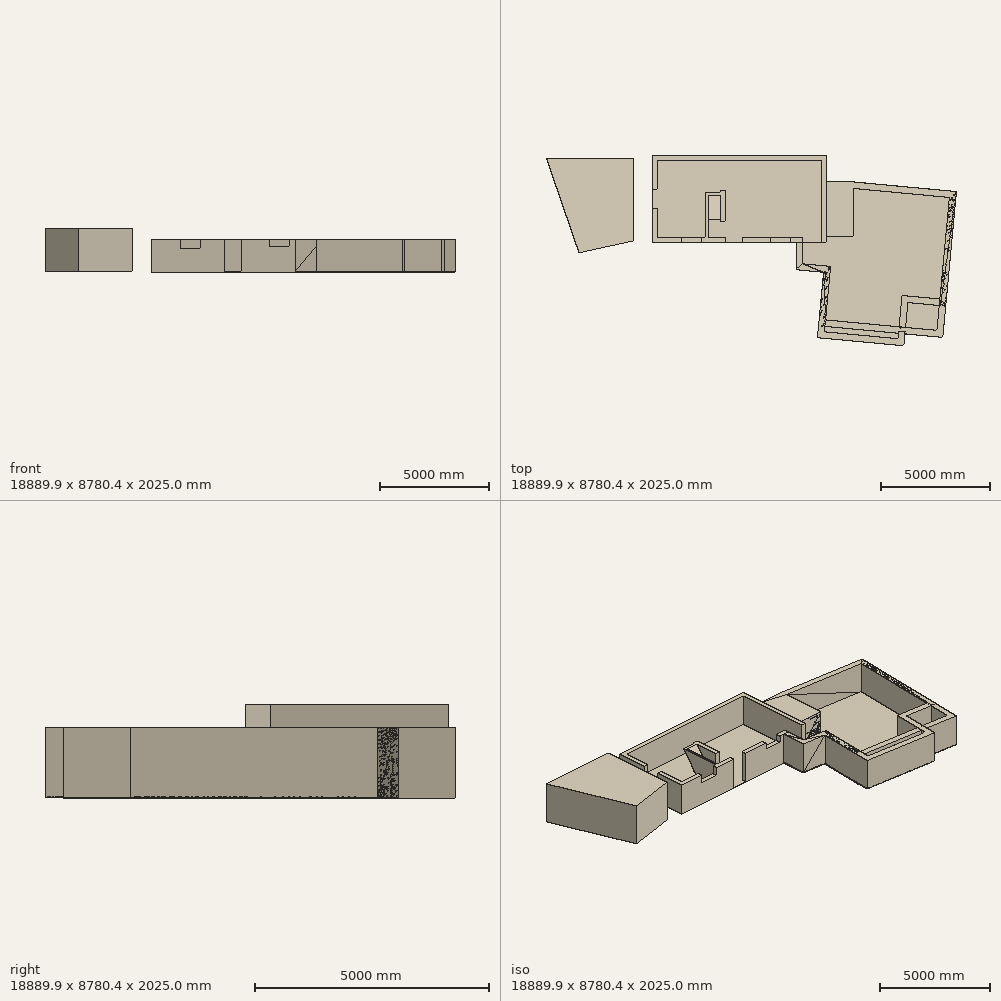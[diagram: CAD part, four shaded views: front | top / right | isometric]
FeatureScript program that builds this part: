
annotation { "Feature Type Name" : "Feature", "Feature Type Description" : "" }
export const myFeature = defineFeature(function(context is Context, id is Id, definition is map)
    precondition{}
    {
        {
            var Q0;
            Q0=qCreatedBy(makeId("Top.planeOp"),FACE);
            var sketch = newSketch(context, id + "F0", { "sketchPlane" : qUnion([Q0])});
            skLineSegment(sketch, "E0.bottom", {"start": v(0, 0) * mm, "end": v(8000, 0) * mm});
            skLineSegment(sketch, "E0.top", {"start": v(0, 4000) * mm, "end": v(8000, 4000) * mm});
            skLineSegment(sketch, "E0.left", {"start": v(0, 0) * mm, "end": v(0, 4000) * mm});
            skLineSegment(sketch, "E0.right", {"start": v(8000, 0) * mm, "end": v(8000, 4000) * mm});
            skPoint(sketch, "E1", {"position": v(8000, 3790) * mm});
            skPoint(sketch, "E2", {"position": v(8781.4, 3726.12) * mm});
            skLineSegment(sketch, "E3", {"start": v(8000, 3790) * mm, "end": v(8781.4, 3726.12) * mm});
            skPoint(sketch, "E4", {"position": v(8821.2, 4094.98) * mm});
            skLineSegment(sketch, "E5", {"start": v(8781.4, 3726.12) * mm, "end": v(8821.2, 4094.98) * mm});
            skPoint(sketch, "E6", {"position": v(11874.29, 3808.86) * mm});
            skPoint(sketch, "E7", {"position": v(11736, -546) * mm});
            skPoint(sketch, "E8", {"position": v(8636, -546) * mm});
            skPoint(sketch, "E9", {"position": v(8636, 269) * mm});
            skPoint(sketch, "E10", {"position": v(8000, 269) * mm});
            skLineSegment(sketch, "E11", {"start": v(8821.2, 4094.98) * mm, "end": v(11874.29, 3808.86) * mm});
            skLineSegment(sketch, "E12", {"start": v(11874.29, 3808.86) * mm, "end": v(11736, -546) * mm});
            skLineSegment(sketch, "E13", {"start": v(11736, -546) * mm, "end": v(8636, -546) * mm});
            skLineSegment(sketch, "E14", {"start": v(8636, -546) * mm, "end": v(8636, 269) * mm});
            skLineSegment(sketch, "E15", {"start": v(8636, 269) * mm, "end": v(8000, 269) * mm});
            skLineSegment(sketch, "E16", {"start": v(8636, 269) * mm, "end": v(9250, 269) * mm});
            skLineSegment(sketch, "E17", {"start": v(9250, 269) * mm, "end": v(9250, 990) * mm});
            skLineSegment(sketch, "E18", {"start": v(9250, 990) * mm, "end": v(9763, 990) * mm});
            skLineSegment(sketch, "E19", {"start": v(9763, 990) * mm, "end": v(9763, 1490) * mm});
            skLineSegment(sketch, "E20", {"start": v(9763, 1490) * mm, "end": v(9250, 1490) * mm});
            skLineSegment(sketch, "E21", {"start": v(9250, 1490) * mm, "end": v(9250, 2769) * mm});
            skLineSegment(sketch, "E22", {"start": v(9250, 2769) * mm, "end": v(8000, 2769) * mm});
            skLineSegment(sketch, "E23", {"start": v(11874.29, 3808.86) * mm, "end": v(14303.17, 3581.23) * mm});
            skLineSegment(sketch, "E24", {"start": v(14303.17, 3581.23) * mm, "end": v(14605.98, 6812.25) * mm});
            skLineSegment(sketch, "E25", {"start": v(8821.2, 4094.98) * mm, "end": v(9124, 7326) * mm});
            skPoint(sketch, "E26", {"position": v(6355, 0) * mm});
            skPoint(sketch, "E27", {"position": v(5445, 0) * mm});
            skPoint(sketch, "E28", {"position": v(4130, 0) * mm});
            skPoint(sketch, "E29", {"position": v(3370, 0) * mm});
            skPoint(sketch, "E30", {"position": v(2265, 0) * mm});
            skPoint(sketch, "E31", {"position": v(1305, 0) * mm});
            skLineSegment(sketch, "E32", {"start": v(9124, 7326) * mm, "end": v(14605.98, 6812.25) * mm});
            skPoint(sketch, "E33", {"position": v(0, 2435) * mm});
            skPoint(sketch, "E34", {"position": v(0, 1565) * mm});
            skSolve(sketch);
        }
        {
            var Q0;
            Q0=qCreatedBy(makeId("Top.planeOp"),FACE);
            var sketch = newSketch(context, id + "F1", { "sketchPlane" : qUnion([Q0])});
            skLineSegment(sketch, "E35", {"start": v(9250, 2769) * mm, "end": v(13993.04, 2324.5) * mm});
            skLineSegment(sketch, "E36", {"start": v(13993.04, 2324.5) * mm, "end": v(13363.21, -4396.06) * mm});
            skLineSegment(sketch, "E37", {"start": v(13363.21, -4396.06) * mm, "end": v(7638.3, -3859.53) * mm});
            skLineSegment(sketch, "E38", {"start": v(7638.3, -3859.53) * mm, "end": v(7869.37, -1393.9) * mm});
            skLineSegment(sketch, "E39", {"start": v(9250, 2769) * mm, "end": v(8000, 2769) * mm});
            skLineSegment(sketch, "E40", {"start": v(8000, 2769) * mm, "end": v(8000, 0) * mm});
            skLineSegment(sketch, "E41", {"start": v(6600, 0) * mm, "end": v(8000, 0) * mm});
            skLineSegment(sketch, "E42", {"start": v(6600, 0) * mm, "end": v(6600, -1274.93) * mm});
            skLineSegment(sketch, "E43", {"start": v(6600, -1274.93) * mm, "end": v(7869.37, -1393.9) * mm});
            skSolve(sketch);
        }
        {
            var Q0;
            Q0=qCreatedBy(makeId("Top.planeOp"),FACE);
            var sketch = newSketch(context, id + "F2", { "sketchPlane" : qUnion([Q0])});
            skLineSegment(sketch, "E44.0", {"start": v(9250, 2467.69) * mm, "end": v(13666.36, 2053.8) * mm});
            skLineSegment(sketch, "E44.1", {"start": v(13666.36, 2053.8) * mm, "end": v(13092.51, -4069.37) * mm});
            skLineSegment(sketch, "E44.2", {"start": v(6900, 0) * mm, "end": v(6900, -1001.73) * mm});
            skLineSegment(sketch, "E44.3", {"start": v(6900, -1001.73) * mm, "end": v(8196.05, -1123.2) * mm});
            skLineSegment(sketch, "E44.4", {"start": v(7964.98, -3588.83) * mm, "end": v(8196.05, -1123.2) * mm});
            skLineSegment(sketch, "E44.5", {"start": v(13092.51, -4069.37) * mm, "end": v(7964.98, -3588.83) * mm});
            skLineSegment(sketch, "E45.0", {"start": v(9250, 2769) * mm, "end": v(13993.04, 2324.5) * mm});
            skLineSegment(sketch, "E46.0", {"start": v(13993.04, 2324.5) * mm, "end": v(13363.21, -4396.06) * mm});
            skLineSegment(sketch, "E47.0", {"start": v(13363.21, -4396.06) * mm, "end": v(7638.3, -3859.53) * mm});
            skLineSegment(sketch, "E48.0", {"start": v(7638.3, -3859.53) * mm, "end": v(7869.37, -1393.9) * mm});
            skLineSegment(sketch, "E49.0", {"start": v(6600, -1274.93) * mm, "end": v(7869.37, -1393.9) * mm});
            skLineSegment(sketch, "E50.0", {"start": v(6600, 0) * mm, "end": v(6600, -1274.93) * mm});
            skLineSegment(sketch, "E51", {"start": v(6600, 0) * mm, "end": v(6900, 0) * mm});
            skLineSegment(sketch, "E52", {"start": v(9250, 2467.69) * mm, "end": v(9250, 269) * mm});
            skLineSegment(sketch, "E53", {"start": v(9250, 269) * mm, "end": v(8000, 269) * mm});
            skLineSegment(sketch, "E54", {"start": v(8000, 269) * mm, "end": v(8000, 2769) * mm});
            skLineSegment(sketch, "E55", {"start": v(8000, 2769) * mm, "end": v(9250, 2769) * mm});
            skSolve(sketch);
        }
        {
            var Q0;
            Q0=qCreatedBy(makeId("Top.planeOp"),FACE);
            var sketch = newSketch(context, id + "F3", { "sketchPlane" : qUnion([Q0])});
            skLineSegment(sketch, "E56.0", {"start": v(0, 4000) * mm, "end": v(8000, 4000) * mm});
            skLineSegment(sketch, "E57.0", {"start": v(0, 0) * mm, "end": v(0, 4000) * mm});
            skLineSegment(sketch, "E58.0", {"start": v(0, 0) * mm, "end": v(6900, 0) * mm});
            skLineSegment(sketch, "E59.0", {"start": v(8000, 0) * mm, "end": v(8000, 4000) * mm});
            skLineSegment(sketch, "E60.0", {"start": v(230, 3770) * mm, "end": v(7770, 3770) * mm});
            skLineSegment(sketch, "E60.1", {"start": v(230, 230) * mm, "end": v(230, 3770) * mm});
            skLineSegment(sketch, "E60.2", {"start": v(230, 230) * mm, "end": v(2430, 230) * mm});
            skLineSegment(sketch, "E60.3", {"start": v(7770, 0) * mm, "end": v(7770, 3770) * mm});
            skLineSegment(sketch, "E61.1", {"start": v(0, 4000) * mm, "end": v(0, 0) * mm});
            skLineSegment(sketch, "E61.2", {"start": v(8000, 269) * mm, "end": v(8000, 2769) * mm});
            skLineSegment(sketch, "E61.3", {"start": v(8000, 2769) * mm, "end": v(8000, 3790) * mm});
            skLineSegment(sketch, "E61.4", {"start": v(8000, 3790) * mm, "end": v(8000, 4000) * mm});
            skLineSegment(sketch, "E61.5", {"start": v(8000, 0) * mm, "end": v(8000, 269) * mm});
            skLineSegment(sketch, "E61.6", {"start": v(8000, 4000) * mm, "end": v(0, 4000) * mm});
            skLineSegment(sketch, "E62", {"start": v(6900, 0) * mm, "end": v(6900, 230) * mm});
            skLineSegment(sketch, "E63.trimOffspring", {"start": v(8000, 0) * mm, "end": v(8000, 0) * mm});
            skLineSegment(sketch, "E64.trimOffspring", {"start": v(7770, 0) * mm, "end": v(8000, 0) * mm});
            skLineSegment(sketch, "E65", {"start": v(3370, 2370) * mm, "end": v(3370, 940) * mm});
            skLineSegment(sketch, "E66", {"start": v(3140, 2370) * mm, "end": v(3370, 2370) * mm});
            skLineSegment(sketch, "E67", {"start": v(2430, 230) * mm, "end": v(2430, 1170) * mm});
            skLineSegment(sketch, "E68", {"start": v(2545, 1170) * mm, "end": v(2545, 230) * mm});
            skLineSegment(sketch, "E69.trimOffspring", {"start": v(3140, 940) * mm, "end": v(3140, 2370) * mm});
            skLineSegment(sketch, "E70.trimOffspring", {"start": v(2545, 230) * mm, "end": v(6900, 230) * mm});
            skPoint(sketch, "E71.start.orphan", {"position": v(2545, 230) * mm});
            skLineSegment(sketch, "E72", {"start": v(2430, 1170) * mm, "end": v(2545, 1170) * mm});
            skLineSegment(sketch, "E73", {"start": v(3140, 940) * mm, "end": v(3370, 940) * mm});
            skSolve(sketch);
        }
        {
            var Q0;
            Q0 = qSketchRegion(id + "F2", true);
            extrude(context, id + "F4", {"entities" : qUnion([Q0]), "depth" : 1500 * mm});
        }
        {
            var Q0;
            Q0 = qSketchRegion(id + "F3", true);
            extrude(context, id + "F5", {"entities" : qUnion([Q0]), "depth" : 1500 * mm});
        }
        {
            var Q0;
            Q0=makeQuery(id+"F5.opExtrude","SWEPT_FACE",FACE,{"disambiguationData":[OSD([sQuery(id+"F3.wireOp",EDGE,"E58.0")])]});
            var sketch = newSketch(context, id + "F6", { "sketchPlane" : qUnion([Q0])});
            skLineSegment(sketch, "E74.bottom", {"start": v(3370, 0) * mm, "end": v(4130, 0) * mm});
            skLineSegment(sketch, "E74.top", {"start": v(3370, 1500) * mm, "end": v(4130, 1500) * mm});
            skLineSegment(sketch, "E74.left", {"start": v(3370, 0) * mm, "end": v(3370, 1500) * mm});
            skLineSegment(sketch, "E74.right", {"start": v(4130, 0) * mm, "end": v(4130, 1500) * mm});
            skLineSegment(sketch, "E75.bottom", {"start": v(5445, 1500) * mm, "end": v(6355, 1500) * mm});
            skLineSegment(sketch, "E75.top", {"start": v(5445, 1175) * mm, "end": v(6355, 1175) * mm});
            skLineSegment(sketch, "E75.left", {"start": v(5445, 1500) * mm, "end": v(5445, 1175) * mm});
            skLineSegment(sketch, "E75.right", {"start": v(6355, 1500) * mm, "end": v(6355, 1175) * mm});
            skLineSegment(sketch, "E76.bottom", {"start": v(1305, 1500) * mm, "end": v(2265, 1500) * mm});
            skLineSegment(sketch, "E76.top", {"start": v(1305, 1098) * mm, "end": v(2265, 1098) * mm});
            skLineSegment(sketch, "E76.left", {"start": v(1305, 1500) * mm, "end": v(1305, 1098) * mm});
            skLineSegment(sketch, "E76.right", {"start": v(2265, 1500) * mm, "end": v(2265, 1098) * mm});
            skSolve(sketch);
        }
        {
            var Q0;
            Q0 = qSketchRegion(id + "F6", true);
            extrude(context, id + "F7", {"entities" : qUnion([Q0]), "operationType" : NewBodyOperationType.REMOVE, "endBound" : BoundingType.UP_TO_NEXT, "oppositeDirection" : true, "depth" : 25 * mm});
        }
        {
            var Q0;
            {var subQ1=sQuery(id+"F0.wireOp",EDGE,"E0.bottom");Q0=makeQuery(id+"F0.imprint","IMPRINT",FACE,{"disambiguationData":[TD([[makeQuery(id+"F0.imprint","IMPRINT",EDGE,{"derivedFrom":subQ1}),1.0]])]});}
            extrude(context, id + "F8", {"entities" : qUnion([Q0]), "oppositeDirection" : true, "depth" : 25 * mm});
        }
        {
            var Q0;
            Q0=makeQuery(id+"F8.opExtrude","SWEPT_BODY",BODY,{"disambiguationData":[OSD([sQuery(id+"F0.wireOp",EDGE,"E0.bottom"),sQuery(id+"F0.wireOp",EDGE,"E0.top"),sQuery(id+"F0.wireOp",EDGE,"E0.left"),sQuery(id+"F0.wireOp",EDGE,"E0.right")])]});
            var Q1;
            Q1=makeQuery(id+"F7.boolean.opBoolean","SPLIT",BODY,{"disambiguationData":[OD(1.0)],"derivedFrom":makeQuery(id+"F5.opExtrude","SWEPT_BODY",BODY,{"disambiguationData":[OSD([sQuery(id+"F3.wireOp",EDGE,"E60.0"),sQuery(id+"F3.wireOp",EDGE,"E60.1"),sQuery(id+"F3.wireOp",EDGE,"E60.2"),sQuery(id+"F3.wireOp",EDGE,"E60.3"),sQuery(id+"F3.wireOp",EDGE,"E58.0"),sQuery(id+"F3.wireOp",EDGE,"E61.1"),sQuery(id+"F3.wireOp",EDGE,"E61.2"),sQuery(id+"F3.wireOp",EDGE,"E61.3"),sQuery(id+"F3.wireOp",EDGE,"E61.4"),sQuery(id+"F3.wireOp",EDGE,"E61.5"),sQuery(id+"F3.wireOp",EDGE,"E61.6"),sQuery(id+"F3.wireOp",EDGE,"E62"),sQuery(id+"F3.wireOp",EDGE,"E64.trimOffspring")])]})});
            var Q2;
            Q2=makeQuery(id+"F7.boolean.opBoolean","SPLIT",BODY,{"disambiguationData":[OD(0.0)],"derivedFrom":makeQuery(id+"F5.opExtrude","SWEPT_BODY",BODY,{"disambiguationData":[OSD([sQuery(id+"F3.wireOp",EDGE,"E60.0"),sQuery(id+"F3.wireOp",EDGE,"E60.1"),sQuery(id+"F3.wireOp",EDGE,"E60.2"),sQuery(id+"F3.wireOp",EDGE,"E60.3"),sQuery(id+"F3.wireOp",EDGE,"E58.0"),sQuery(id+"F3.wireOp",EDGE,"E61.1"),sQuery(id+"F3.wireOp",EDGE,"E61.2"),sQuery(id+"F3.wireOp",EDGE,"E61.3"),sQuery(id+"F3.wireOp",EDGE,"E61.4"),sQuery(id+"F3.wireOp",EDGE,"E61.5"),sQuery(id+"F3.wireOp",EDGE,"E61.6"),sQuery(id+"F3.wireOp",EDGE,"E62"),sQuery(id+"F3.wireOp",EDGE,"E64.trimOffspring")])]})});
            booleanBodies(context, id + "F9", {"operationType" : BooleanOperationType.UNION, "tools" : qUnion([Q0, Q1, Q2])});
        }
        {
            var Q0;
            Q0=makeQuery(id+"F1.imprint","IMPRINT",FACE,{"disambiguationData":[TD([[makeQuery(id+"F1.imprint","IMPRINT",EDGE,{"derivedFrom":sQuery(id+"F1.wireOp",EDGE,"E35")}),-1.0]])]});
            extrude(context, id + "F10", {"entities" : qUnion([Q0]), "oppositeDirection" : true, "depth" : 25 * mm});
        }
        {
            var Q0;
            Q0=makeQuery(id+"F5.opExtrude","SWEPT_FACE",FACE,{"disambiguationData":[OSD([sQuery(id+"F3.wireOp",EDGE,"E67")])]});
            var sketch = newSketch(context, id + "F11", { "sketchPlane" : qUnion([Q0])});
            skLineSegment(sketch, "E77", {"start": v(-1170, 0) * mm, "end": v(-1170, 1500) * mm});
            skLineSegment(sketch, "E78", {"start": v(-1170, 1500) * mm, "end": v(-2295, 1500) * mm});
            skLineSegment(sketch, "E79", {"start": v(-2295, 1500) * mm, "end": v(-1170, 0) * mm});
            skPoint(sketch, "E80", {"position": v(-2370, 1600) * mm});
            skSolve(sketch);
        }
        {
            var Q0;
            Q0 = qSketchRegion(id + "F11", true);
            var Q1;
            Q1=makeQuery(id+"F5.opExtrude","SWEPT_FACE",FACE,{"disambiguationData":[OSD([sQuery(id+"F3.wireOp",EDGE,"E68")])]});
            extrude(context, id + "F12", {"entities" : qUnion([Q0]), "operationType" : NewBodyOperationType.ADD, "endBound" : BoundingType.UP_TO_SURFACE, "oppositeDirection" : true, "endBoundEntityFace" : qUnion([Q1]), "depth" : 25 * mm});
        }
        {
            var Q0;
            {var subQ0=sQuery(id+"F3.wireOp",EDGE,"E68");Q0=makeQuery(id+"F12.boolean.opBoolean","MERGE",FACE,{"derivedFrom":[makeQuery(id+"F5.opExtrude","SWEPT_FACE",FACE,{"disambiguationData":[OSD([subQ0])]}),makeQuery(id+"F12.opExtrude","CAP_FACE",FACE,{"disambiguationData":[OSD([subQ0])],"isStart":false})]});}
            var sketch = newSketch(context, id + "F13", { "sketchPlane" : qUnion([Q0])});
            skLineSegment(sketch, "E81", {"start": v(2295, 1500) * mm, "end": v(2151.25, 1500) * mm});
            skLineSegment(sketch, "E82", {"start": v(2151.25, 1500) * mm, "end": v(1026.25, 0) * mm});
            skLineSegment(sketch, "E83", {"start": v(1026.25, 0) * mm, "end": v(1170, 0) * mm});
            skLineSegment(sketch, "E84", {"start": v(1170, 0) * mm, "end": v(2295, 1500) * mm});
            skSolve(sketch);
        }
        {
            var Q0;
            Q0 = qSketchRegion(id + "F13", true);
            extrude(context, id + "F14", {"entities" : qUnion([Q0]), "operationType" : NewBodyOperationType.ADD, "endBound" : BoundingType.UP_TO_NEXT, "depth" : 25 * mm});
        }
        {
            var Q0;
            Q0=makeQuery(id+"F9.opBoolean","MERGE",FACE,{"derivedFrom":[makeQuery(id+"F5.opExtrude","SWEPT_FACE",FACE,{"disambiguationData":[OSD([sQuery(id+"F3.wireOp",EDGE,"E61.1")])]}),makeQuery(id+"F8.opExtrude","SWEPT_FACE",FACE,{"disambiguationData":[OSD([sQuery(id+"F0.wireOp",EDGE,"E0.left")])]})]});
            var sketch = newSketch(context, id + "F15", { "sketchPlane" : qUnion([Q0])});
            skLineSegment(sketch, "E85.bottom", {"start": v(-1565, 0) * mm, "end": v(-2435, 0) * mm});
            skLineSegment(sketch, "E85.top", {"start": v(-1565, 1500) * mm, "end": v(-2435, 1500) * mm});
            skLineSegment(sketch, "E85.left", {"start": v(-1565, 0) * mm, "end": v(-1565, 1500) * mm});
            skLineSegment(sketch, "E85.right", {"start": v(-2435, 0) * mm, "end": v(-2435, 1500) * mm});
            skSolve(sketch);
        }
        {
            var Q0;
            Q0=makeQuery(id+"F15.imprint","IMPRINT",FACE,{"disambiguationData":[TD([[makeQuery(id+"F15.imprint","IMPRINT",EDGE,{"derivedFrom":sQuery(id+"F15.wireOp",EDGE,"E85.bottom")}),-1.0]])]});
            extrude(context, id + "F16", {"entities" : qUnion([Q0]), "operationType" : NewBodyOperationType.REMOVE, "oppositeDirection" : true, "depth" : 230 * mm});
        }
        {
            var Q0;
            Q0=qCreatedBy(makeId("Top.planeOp"),FACE);
            var sketch = newSketch(context, id + "F17", { "sketchPlane" : qUnion([Q0])});
            skLineSegment(sketch, "E86", {"start": v(9250, 2769) * mm, "end": v(13993.04, 2324.5) * mm});
            skLineSegment(sketch, "E87", {"start": v(13993.04, 2324.5) * mm, "end": v(13498.5, -2952.38) * mm});
            skLineSegment(sketch, "E88", {"start": v(13498.5, -2952.38) * mm, "end": v(11756.14, -2789.1) * mm});
            skLineSegment(sketch, "E89", {"start": v(11756.14, -2789.1) * mm, "end": v(11569.53, -4780.37) * mm});
            skLineSegment(sketch, "E90", {"start": v(11569.53, -4780.37) * mm, "end": v(7586.98, -4407.13) * mm});
            skLineSegment(sketch, "E91", {"start": v(7586.98, -4407.13) * mm, "end": v(7869.37, -1393.9) * mm});
            skLineSegment(sketch, "E92", {"start": v(7869.37, -1393.9) * mm, "end": v(6600, -1274.93) * mm});
            skLineSegment(sketch, "E93", {"start": v(6600, -1274.93) * mm, "end": v(6600, 0) * mm});
            skLineSegment(sketch, "E94", {"start": v(6600, 0) * mm, "end": v(8000, 0) * mm});
            skLineSegment(sketch, "E95", {"start": v(8000, 0) * mm, "end": v(8000, 269) * mm});
            skLineSegment(sketch, "E96", {"start": v(8000, 269) * mm, "end": v(8000, 2769) * mm});
            skLineSegment(sketch, "E97", {"start": v(8000, 2769) * mm, "end": v(9250, 2769) * mm});
            skSolve(sketch);
        }
        {
            var Q0;
            Q0 = qSketchRegion(id + "F17", true);
            extrude(context, id + "F18", {"entities" : qUnion([Q0]), "depth" : 25 * mm, "offsetDistance" : 25 * mm});
        }
        {
            var Q0;
            Q0=qCreatedBy(makeId("Top.planeOp"),FACE);
            var sketch = newSketch(context, id + "F19", { "sketchPlane" : qUnion([Q0])});
            skLineSegment(sketch, "E98.0", {"start": v(6900, 0) * mm, "end": v(6900, -1001.73) * mm});
            skLineSegment(sketch, "E98.1", {"start": v(6900, -1001.73) * mm, "end": v(8196.05, -1123.2) * mm});
            skLineSegment(sketch, "E98.2", {"start": v(9250, 2467.69) * mm, "end": v(13666.36, 2053.8) * mm});
            skLineSegment(sketch, "E99", {"start": v(8000, 269) * mm, "end": v(9250, 269) * mm});
            skLineSegment(sketch, "E100", {"start": v(9250, 269) * mm, "end": v(9250, 2467.69) * mm});
            skLineSegment(sketch, "E101.0", {"start": v(9250, 2769) * mm, "end": v(8000, 2769) * mm});
            skLineSegment(sketch, "E102.0", {"start": v(9250, 2769) * mm, "end": v(13993.04, 2324.5) * mm});
            skLineSegment(sketch, "E103.0", {"start": v(6600, -1274.93) * mm, "end": v(7869.37, -1393.9) * mm});
            skLineSegment(sketch, "E104.0", {"start": v(6600, 0) * mm, "end": v(6600, -1274.93) * mm});
            skLineSegment(sketch, "E105", {"start": v(6600, 0) * mm, "end": v(6900, 0) * mm});
            skLineSegment(sketch, "E106", {"start": v(8000, 269) * mm, "end": v(8000, 2769) * mm});
            skLineSegment(sketch, "E107.0", {"start": v(13993.04, 2324.5) * mm, "end": v(13498.5, -2952.38) * mm});
            skLineSegment(sketch, "E108.0", {"start": v(13498.5, -2952.38) * mm, "end": v(11756.14, -2789.1) * mm});
            skLineSegment(sketch, "E109.0", {"start": v(11756.14, -2789.1) * mm, "end": v(11569.53, -4780.37) * mm});
            skLineSegment(sketch, "E110.0", {"start": v(11569.53, -4780.37) * mm, "end": v(7586.98, -4407.13) * mm});
            skLineSegment(sketch, "E111.0", {"start": v(7586.98, -4407.13) * mm, "end": v(7869.37, -1393.9) * mm});
            skLineSegment(sketch, "E112.0", {"start": v(7913.66, -4136.44) * mm, "end": v(8196.05, -1123.2) * mm});
            skLineSegment(sketch, "E112.1", {"start": v(13666.36, 2053.8) * mm, "end": v(13227.8, -2625.7) * mm});
            skLineSegment(sketch, "E112.2", {"start": v(13227.8, -2625.7) * mm, "end": v(11485.44, -2462.4) * mm});
            skLineSegment(sketch, "E112.3", {"start": v(11485.44, -2462.4) * mm, "end": v(11298.83, -4453.68) * mm});
            skLineSegment(sketch, "E112.4", {"start": v(11298.83, -4453.68) * mm, "end": v(7913.66, -4136.44) * mm});
            skSolve(sketch);
        }
        {
            var Q0;
            Q0 = qSketchRegion(id + "F19", true);
            extrude(context, id + "F20", {"entities" : qUnion([Q0]), "depth" : 1500 * mm, "offsetDistance" : 25 * mm});
        }
        {
            var Q0;
            Q0=qCreatedBy(makeId("Top.planeOp"),FACE);
            var sketch = newSketch(context, id + "F21", { "sketchPlane" : qUnion([Q0])});
            skLineSegment(sketch, "E113", {"start": v(-896.87, 48.71) * mm, "end": v(-3396.87, -499.85) * mm});
            skLineSegment(sketch, "E114", {"start": v(-3396.87, -499.85) * mm, "end": v(-4896.87, 3848.71) * mm});
            skLineSegment(sketch, "E115", {"start": v(-4896.87, 3848.71) * mm, "end": v(-896.87, 3848.71) * mm});
            skLineSegment(sketch, "E116", {"start": v(-896.87, 3848.71) * mm, "end": v(-896.87, 48.71) * mm});
            skSolve(sketch);
        }
        {
            var Q0;
            Q0 = qSketchRegion(id + "F21", true);
            extrude(context, id + "F22", {"entities" : qUnion([Q0]), "depth" : 2000 * mm, "offsetDistance" : 25 * mm});
        }
    });
